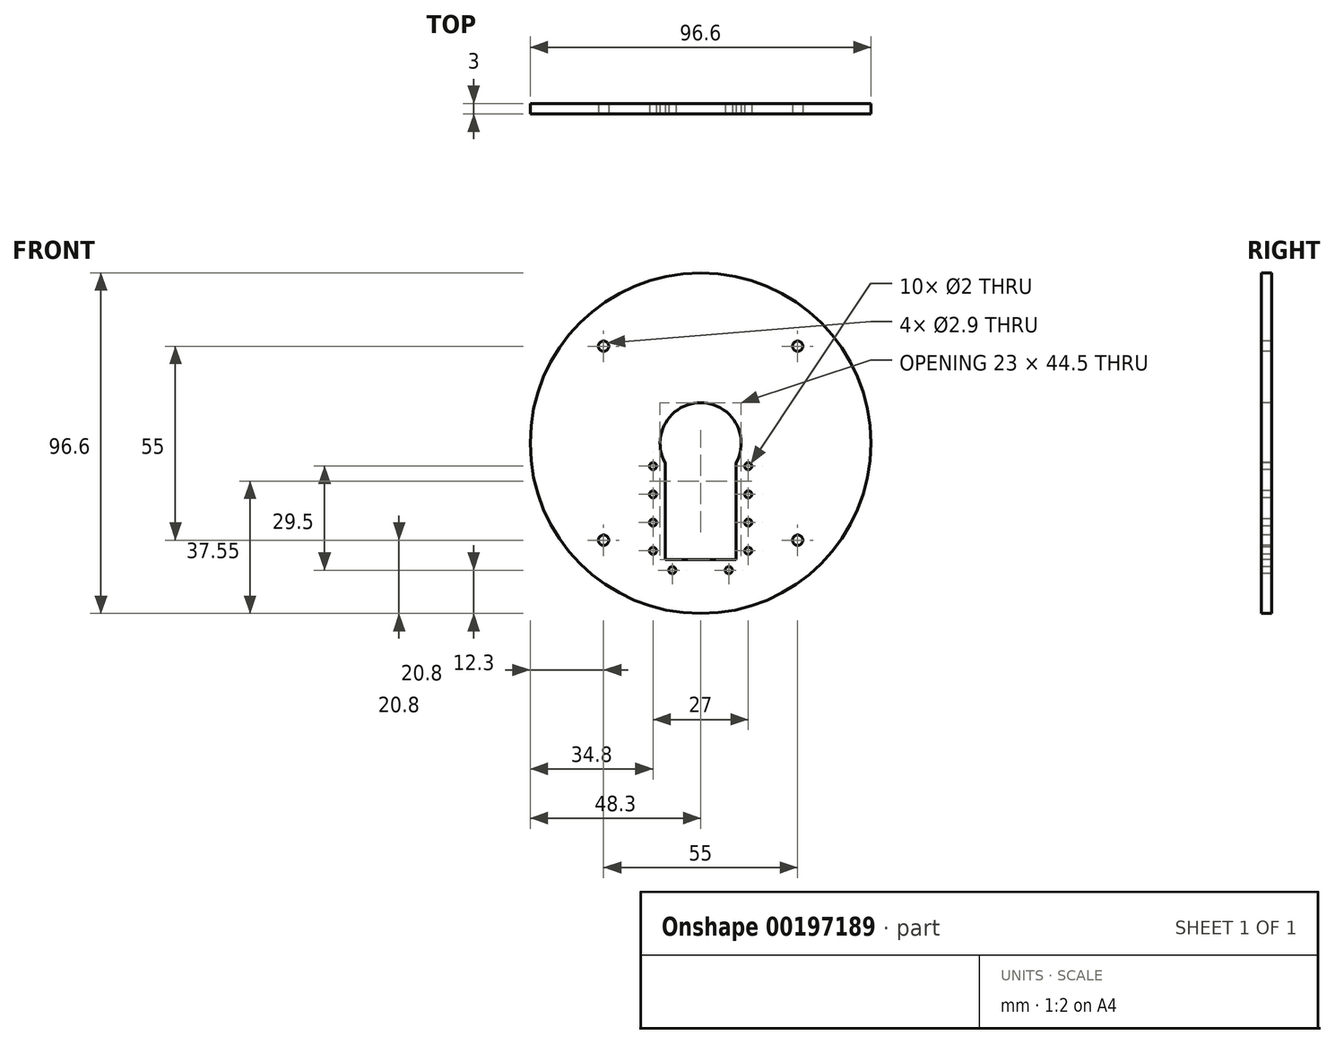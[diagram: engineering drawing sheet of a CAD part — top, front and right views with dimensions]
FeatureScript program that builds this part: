
annotation { "Feature Type Name" : "Feature", "Feature Type Description" : "" }
export const myFeature = defineFeature(function(context is Context, id is Id, definition is map)
    precondition{}
    {
        {
            var Q0;
            Q0=qCreatedBy(makeId("Front.planeOp"),FACE);
            var sketch = newSketch(context, id + "F0", { "sketchPlane" : qUnion([Q0])});
            skCircle(sketch, "E0", {"center": v(0, 0) * mm, "radius": 48.3 * mm});
            skSolve(sketch);
        }
        {
            var Q0;
            Q0=qSketchRegion(id+"F0",true);
            extrude(context, id + "F1", {"entities" : qUnion([Q0]), "depth" : 3 * mm});
        }
        {
            var Q0;
            Q0=makeQuery(id+"F1.opExtrude","CAP_FACE",FACE,{"disambiguationData":[OSD([sQuery(id+"F0.wireOp",EDGE,"E0")])],"isStart":false});
            var sketch = newSketch(context, id + "F2", { "sketchPlane" : qUnion([Q0])});
            skLineSegment(sketch, "E1", {"start": v(-48.3, 0) * mm, "end": v(48.3, 0) * mm, "construction": true});
            skLineSegment(sketch, "E2", {"start": v(0, 0) * mm, "end": v(0, 33.83) * mm, "construction": true});
            skCircle(sketch, "E3", {"center": v(-8, 0) * mm, "radius": 1.25 * mm});
            skCircle(sketch, "E4.MirrorC", {"center": v(8, 0) * mm, "radius": 1.25 * mm});
            skCircle(sketch, "E5", {"center": v(0, 0) * mm, "radius": 2.5 * mm});
            skSolve(sketch);
        }
        {
            var Q0;
            Q0=qSketchRegion(id+"F2",true);
            extrude(context, id + "F3", {"entities" : qUnion([Q0]), "operationType" : NewBodyOperationType.REMOVE, "endBound" : BoundingType.THROUGH_ALL, "oppositeDirection" : true, "depth" : 25 * mm});
        }
        {
            var Q0;
            Q0=makeQuery(id+"F1.opExtrude","CAP_FACE",FACE,{"disambiguationData":[OSD([sQuery(id+"F0.wireOp",EDGE,"E0")])],"isStart":false});
            var sketch = newSketch(context, id + "F4", { "sketchPlane" : qUnion([Q0])});
            skLineSegment(sketch, "E6", {"start": v(0, 0) * mm, "end": v(0, 23.9) * mm, "construction": true});
            skLineSegment(sketch, "E7", {"start": v(0, 0) * mm, "end": v(-31.3, 0) * mm, "construction": true});
            skCircle(sketch, "E8", {"center": v(-27.5, 27.5) * mm, "radius": 1.45 * mm});
            skCircle(sketch, "E9.MirrorC", {"center": v(27.5, 27.5) * mm, "radius": 1.45 * mm});
            skCircle(sketch, "E10.MirrorC", {"center": v(-27.5, -27.5) * mm, "radius": 1.45 * mm});
            skCircle(sketch, "E11.MirrorC", {"center": v(27.5, -27.5) * mm, "radius": 1.45 * mm});
            skSolve(sketch);
        }
        {
            var Q0;
            Q0=qSketchRegion(id+"F4",true);
            extrude(context, id + "F5", {"entities" : qUnion([Q0]), "operationType" : NewBodyOperationType.REMOVE, "endBound" : BoundingType.THROUGH_ALL, "oppositeDirection" : true, "depth" : 25 * mm});
        }
        {
            var Q0;
            Q0=makeQuery(id+"F1.opExtrude","CAP_FACE",FACE,{"disambiguationData":[OSD([sQuery(id+"F0.wireOp",EDGE,"E0")])],"isStart":false});
            var sketch = newSketch(context, id + "F6", { "sketchPlane" : qUnion([Q0])});
            skLineSegment(sketch, "E12", {"start": v(0, 0) * mm, "end": v(0, -47.3) * mm, "construction": true});
            skLineSegment(sketch, "E13.bottom", {"start": v(10.05, -33) * mm, "end": v(-10.05, -33) * mm});
            skLineSegment(sketch, "E13.top", {"start": v(10.05, 0) * mm, "end": v(-10.05, 0) * mm});
            skLineSegment(sketch, "E13.left", {"start": v(10.05, -33) * mm, "end": v(10.05, 0) * mm});
            skLineSegment(sketch, "E13.right", {"start": v(-10.05, -33) * mm, "end": v(-10.05, 0) * mm});
            skPoint(sketch, "E13.middle", {"position": v(0, -16.5) * mm});
            skCircle(sketch, "E14", {"center": v(-13.5, -6.5) * mm, "radius": 1 * mm});
            skLineSegment(sketch, "E15", {"start": v(0, 0) * mm, "end": v(-21.48, 0) * mm, "construction": true});
            skCircle(sketch, "E16.0.1.0", {"center": v(-13.5, -14.5) * mm, "radius": 1 * mm});
            skCircle(sketch, "E16.0.2.0", {"center": v(-13.5, -22.5) * mm, "radius": 1 * mm});
            skCircle(sketch, "E16.0.3.0", {"center": v(-13.5, -30.5) * mm, "radius": 1 * mm});
            skLineSegment(sketch, "E16.direction1", {"start": v(-13.5, -6.5) * mm, "end": v(11.73, -6.5) * mm, "construction": true});
            skLineSegment(sketch, "E16.direction2", {"start": v(-13.5, -6.5) * mm, "end": v(-13.5, -14.5) * mm, "construction": true});
            skCircle(sketch, "E17.MirrorC", {"center": v(13.5, -6.5) * mm, "radius": 1 * mm});
            skCircle(sketch, "E18.MirrorC", {"center": v(13.5, -14.5) * mm, "radius": 1 * mm});
            skCircle(sketch, "E19.MirrorC", {"center": v(13.5, -22.5) * mm, "radius": 1 * mm});
            skCircle(sketch, "E20.MirrorC", {"center": v(13.5, -30.5) * mm, "radius": 1 * mm});
            skCircle(sketch, "E21", {"center": v(0, 0) * mm, "radius": 11.5 * mm});
            skCircle(sketch, "E22", {"center": v(-8, -36) * mm, "radius": 1 * mm});
            skCircle(sketch, "E23.MirrorC", {"center": v(8, -36) * mm, "radius": 1 * mm});
            skSolve(sketch);
        }
        {
            var Q0;
            Q0 = qSketchRegion(id + "F6", true);
            extrude(context, id + "F7", {"entities" : qUnion([Q0]), "operationType" : NewBodyOperationType.REMOVE, "endBound" : BoundingType.THROUGH_ALL, "oppositeDirection" : true, "depth" : 25 * mm});
        }
    });
